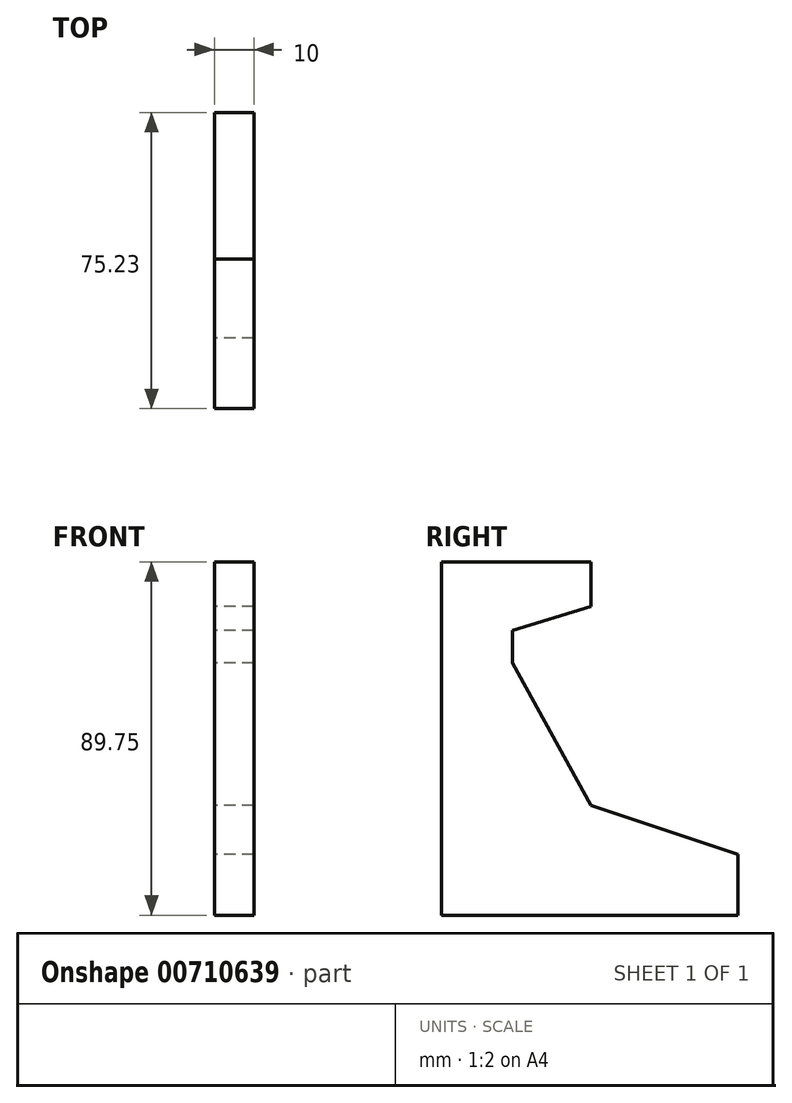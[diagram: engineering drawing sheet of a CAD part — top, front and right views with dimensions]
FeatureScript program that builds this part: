
annotation { "Feature Type Name" : "Feature", "Feature Type Description" : "" }
export const myFeature = defineFeature(function(context is Context, id is Id, definition is map)
    precondition{}
    {
        {
            var Q0;
            Q0=qCreatedBy(makeId("Right.planeOp"),FACE);
            var sketch = newSketch(context, id + "F0", { "sketchPlane" : qUnion([Q0])});
            skLineSegment(sketch, "E0", {"start": v(-37.9, 41.72) * mm, "end": v(-37.9, -48.03) * mm});
            skLineSegment(sketch, "E1", {"start": v(-37.9, -48.03) * mm, "end": v(37.33, -48.03) * mm});
            skLineSegment(sketch, "E2", {"start": v(37.33, -48.03) * mm, "end": v(37.33, -32.56) * mm});
            skLineSegment(sketch, "E3", {"start": v(37.33, -32.56) * mm, "end": v(0, -20.15) * mm});
            skLineSegment(sketch, "E4", {"start": v(0, -20.15) * mm, "end": v(-19.95, 16.1) * mm});
            skLineSegment(sketch, "E5", {"start": v(-19.95, 16.1) * mm, "end": v(-19.95, 24.35) * mm});
            skLineSegment(sketch, "E6", {"start": v(-19.95, 24.35) * mm, "end": v(0, 30.46) * mm});
            skLineSegment(sketch, "E7", {"start": v(0, 30.46) * mm, "end": v(0, 41.72) * mm});
            skLineSegment(sketch, "E8", {"start": v(0, 41.72) * mm, "end": v(-37.9, 41.72) * mm});
            skSolve(sketch);
        }
        {
            var Q0;
            Q0 = qSketchRegion(id + "F0", true);
            extrude(context, id + "F1", {"entities" : qUnion([Q0]), "depth" : 10 * mm, "offsetDistance" : 25.4 * mm});
        }
    });
